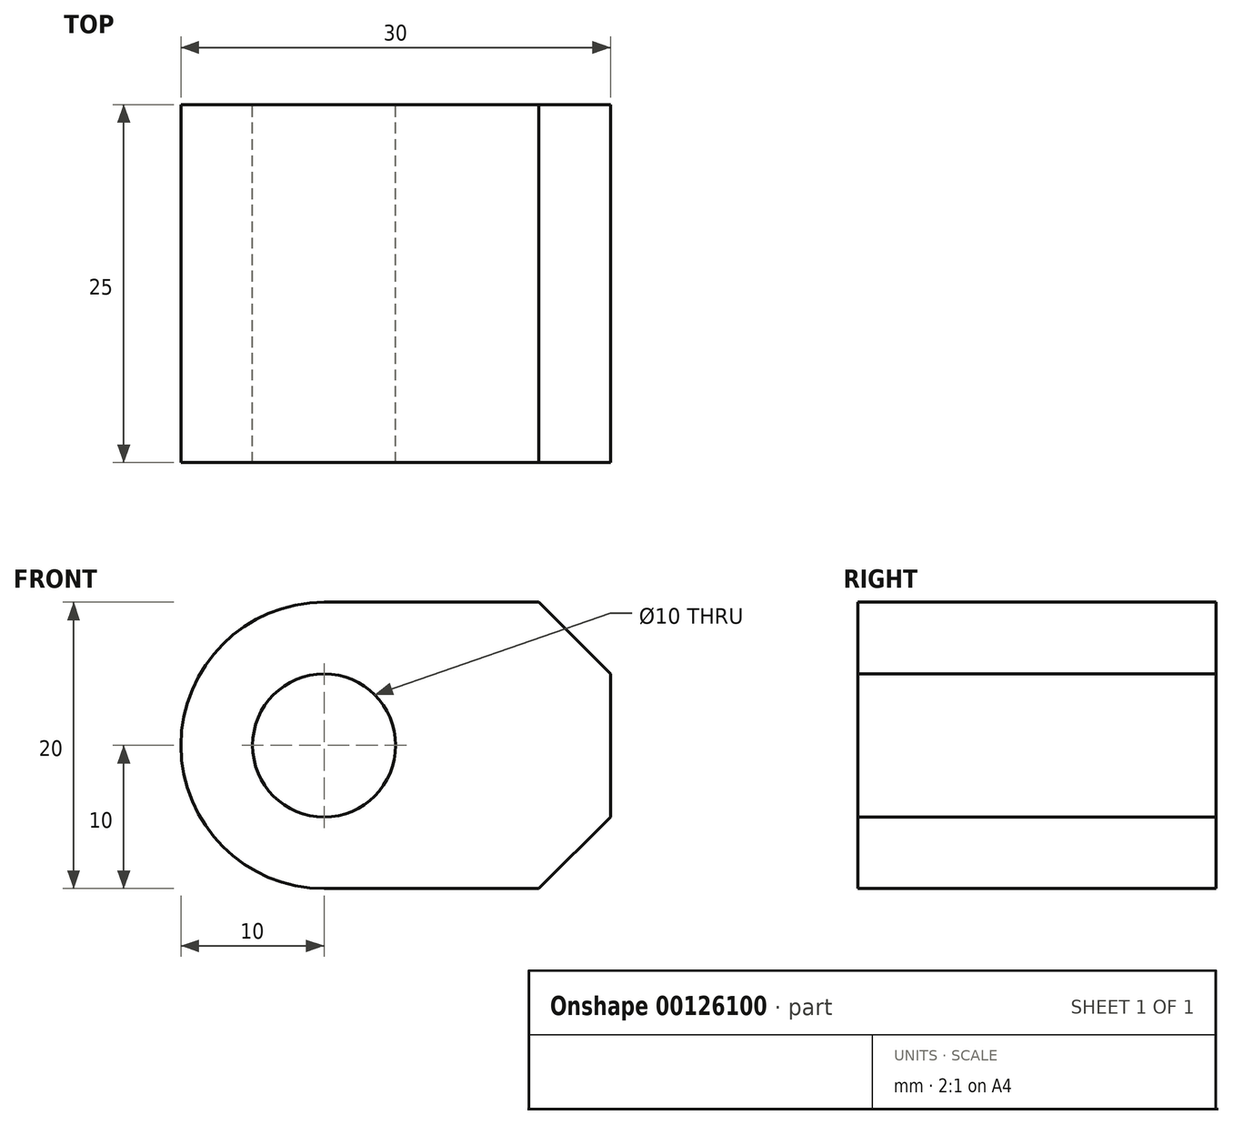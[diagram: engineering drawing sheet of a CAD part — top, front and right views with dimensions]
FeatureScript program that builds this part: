
annotation { "Feature Type Name" : "Feature", "Feature Type Description" : "" }
export const myFeature = defineFeature(function(context is Context, id is Id, definition is map)
    precondition{}
    {
        {
            var Q0;
            Q0=qCreatedBy(makeId("Front.planeOp"),FACE);
            var sketch = newSketch(context, id + "F0", { "sketchPlane" : qUnion([Q0])});
            skLineSegment(sketch, "E0", {"start": v(0, 0) * mm, "end": v(15, 0) * mm});
            skLineSegment(sketch, "E1", {"start": v(15, 0) * mm, "end": v(20, 5) * mm});
            skLineSegment(sketch, "E2", {"start": v(20, 5) * mm, "end": v(20, 15) * mm});
            skLineSegment(sketch, "E3", {"start": v(20, 15) * mm, "end": v(15, 20) * mm});
            skLineSegment(sketch, "E4", {"start": v(15, 20) * mm, "end": v(0, 20) * mm});
            skCircle(sketch, "E5", {"center": v(0, 10) * mm, "radius": 5 * mm});
            skLineSegment(sketch, "E6", {"start": v(20, 7.5) * mm, "end": v(4.33, 7.5) * mm});
            skLineSegment(sketch, "E7", {"start": v(20, 12.5) * mm, "end": v(4.33, 12.5) * mm});
            skArc(sketch, "E8", {"start": v(9.68, 12.5) * mm, "mid": v(-10, 10) * mm, "end": v(9.68, 7.5) * mm});
            skLineSegment(sketch, "E9", {"start": v(-4.33, 12.5) * mm, "end": v(-9.68, 12.5) * mm});
            skLineSegment(sketch, "E10", {"start": v(-4.33, 7.5) * mm, "end": v(-9.68, 7.5) * mm});
            skSolve(sketch);
        }
        {
            var Q0;
            Q0 = qSketchRegion(id + "F0", true);
            extrude(context, id + "F1", {"entities" : qUnion([Q0]), "depth" : 25 * mm});
        }
    });
